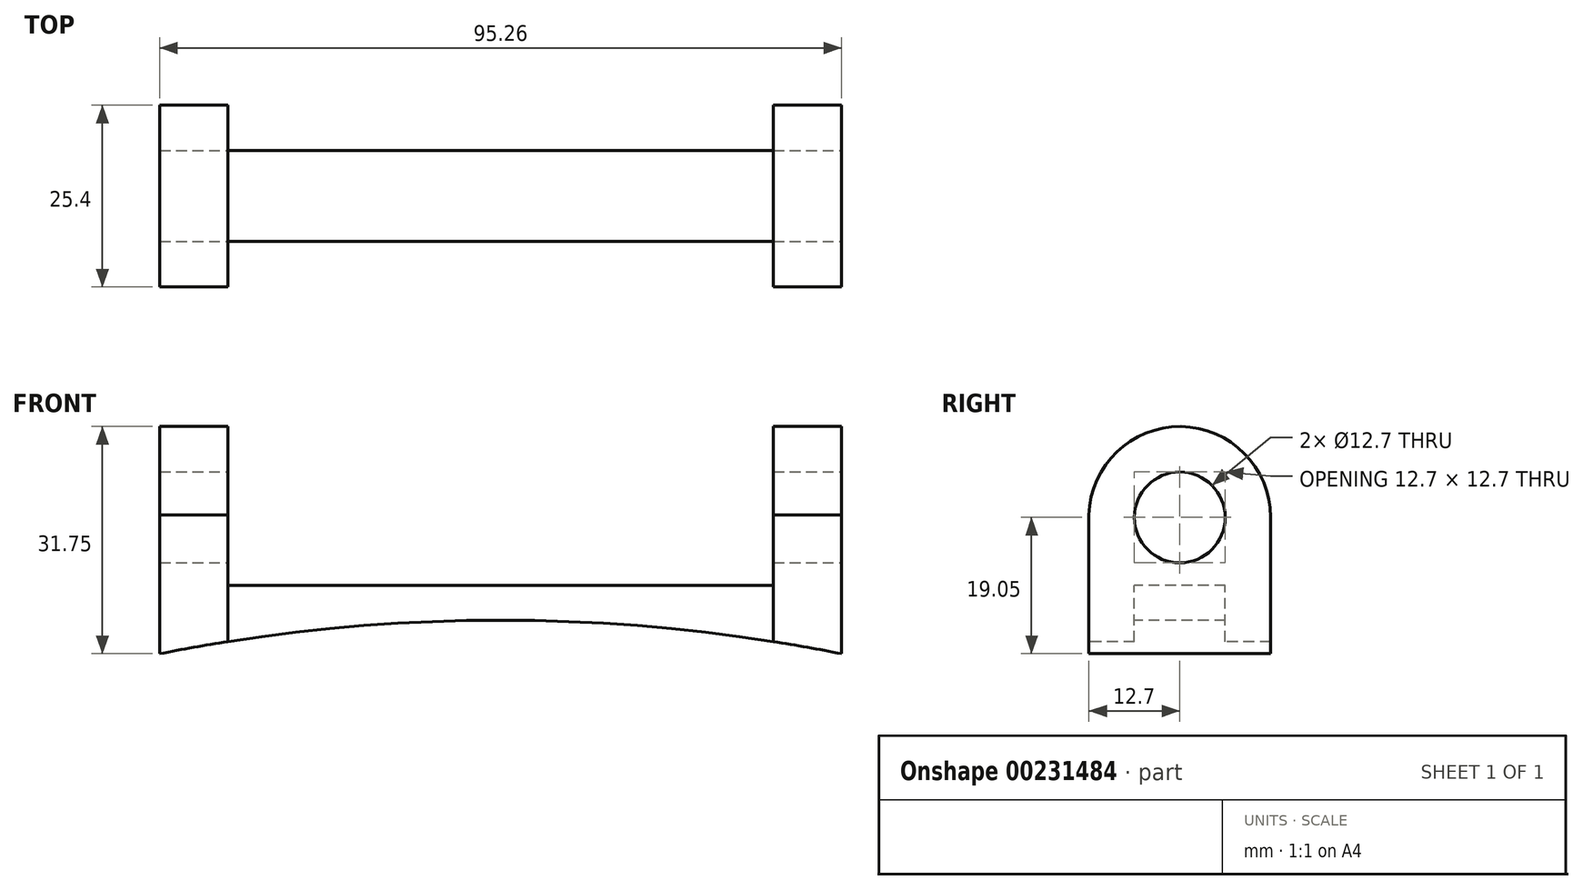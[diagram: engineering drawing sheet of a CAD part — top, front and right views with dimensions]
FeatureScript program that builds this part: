
annotation { "Feature Type Name" : "Feature", "Feature Type Description" : "" }
export const myFeature = defineFeature(function(context is Context, id is Id, definition is map)
    precondition{}
    {
        {
            var Q0;
            Q0=qCreatedBy(makeId("Front.planeOp"),FACE);
            var sketch = newSketch(context, id + "F0", { "sketchPlane" : qUnion([Q0])});
            skLineSegment(sketch, "E0", {"start": v(0, 0) * mm, "end": v(47.63, 0) * mm});
            skLineSegment(sketch, "E1", {"start": v(47.63, 0) * mm, "end": v(47.63, 31.75) * mm});
            skLineSegment(sketch, "E2", {"start": v(47.63, 31.75) * mm, "end": v(-47.62, 31.75) * mm});
            skLineSegment(sketch, "E3", {"start": v(-47.63, 31.75) * mm, "end": v(-47.63, 0) * mm});
            skLineSegment(sketch, "E4", {"start": v(-47.63, 0) * mm, "end": v(0, 0) * mm});
            skSolve(sketch);
        }
        {
            var Q0;
            Q0 = qSketchRegion(id + "F0", true);
            extrude(context, id + "F1", {"entities" : qUnion([Q0]), "depth" : 25.4 * mm});
        }
        {
            var Q0;
            Q0=makeQuery(id+"F1.opExtrude","CAP_FACE",FACE,{"disambiguationData":[OSD([sQuery(id+"F0.wireOp",EDGE,"E0"),sQuery(id+"F0.wireOp",EDGE,"E1"),sQuery(id+"F0.wireOp",EDGE,"E2"),sQuery(id+"F0.wireOp",EDGE,"E3"),sQuery(id+"F0.wireOp",EDGE,"E4")])],"isStart":false});
            var sketch = newSketch(context, id + "F2", { "sketchPlane" : qUnion([Q0])});
            skLineSegment(sketch, "E5.bottom", {"start": v(-38.1, 31.75) * mm, "end": v(38.1, 31.75) * mm});
            skLineSegment(sketch, "E5.top", {"start": v(-38.1, 9.52) * mm, "end": v(38.1, 9.52) * mm});
            skLineSegment(sketch, "E5.left", {"start": v(-38.1, 31.75) * mm, "end": v(-38.1, 9.52) * mm});
            skLineSegment(sketch, "E5.right", {"start": v(38.1, 31.75) * mm, "end": v(38.1, 9.52) * mm});
            skSolve(sketch);
        }
        {
            var Q0;
            Q0 = qSketchRegion(id + "F2", true);
            extrude(context, id + "F3", {"entities" : qUnion([Q0]), "operationType" : NewBodyOperationType.REMOVE, "oppositeDirection" : true, "depth" : 25.4 * mm});
        }
        {
            var Q0;
            Q0=makeQuery(id+"F3.boolean.opBoolean","COPY",FACE,{"derivedFrom":makeQuery(id+"F3.opExtrude","SWEPT_FACE",FACE,{"disambiguationData":[OSD([sQuery(id+"F2.wireOp",EDGE,"E5.top")])]})});
            var sketch = newSketch(context, id + "F4", { "sketchPlane" : qUnion([Q0])});
            skLineSegment(sketch, "E6.bottom", {"start": v(-38.1, 0) * mm, "end": v(38.1, 0) * mm});
            skLineSegment(sketch, "E6.top", {"start": v(-38.1, -6.35) * mm, "end": v(38.1, -6.35) * mm});
            skLineSegment(sketch, "E6.left", {"start": v(-38.1, 0) * mm, "end": v(-38.1, -6.35) * mm});
            skLineSegment(sketch, "E6.right", {"start": v(38.1, 0) * mm, "end": v(38.1, -6.35) * mm});
            skLineSegment(sketch, "E7.bottom", {"start": v(-38.1, -25.4) * mm, "end": v(38.1, -25.4) * mm});
            skLineSegment(sketch, "E7.top", {"start": v(-38.1, -19.05) * mm, "end": v(38.1, -19.05) * mm});
            skLineSegment(sketch, "E7.left", {"start": v(-38.1, -25.4) * mm, "end": v(-38.1, -19.05) * mm});
            skLineSegment(sketch, "E7.right", {"start": v(38.1, -25.4) * mm, "end": v(38.1, -19.05) * mm});
            skSolve(sketch);
        }
        {
            var Q0;
            Q0=makeQuery(id+"F1.opExtrude","CAP_FACE",FACE,{"disambiguationData":[OSD([sQuery(id+"F0.wireOp",EDGE,"E0"),sQuery(id+"F0.wireOp",EDGE,"E1"),sQuery(id+"F0.wireOp",EDGE,"E2"),sQuery(id+"F0.wireOp",EDGE,"E3"),sQuery(id+"F0.wireOp",EDGE,"E4")])],"isStart":false});
            var sketch = newSketch(context, id + "F5", { "sketchPlane" : qUnion([Q0])});
            skArc(sketch, "E8", {"start": v(47.63, 0) * mm, "mid": v(0, 4.68) * mm, "end": v(-47.62, 0) * mm});
            skLineSegment(sketch, "E9", {"start": v(-47.63, 0) * mm, "end": v(47.63, 0) * mm});
            skSolve(sketch);
        }
        {
            var Q0;
            Q0 = qSketchRegion(id + "F5", true);
            extrude(context, id + "F6", {"entities" : qUnion([Q0]), "operationType" : NewBodyOperationType.REMOVE, "oppositeDirection" : true, "depth" : 25.4 * mm});
        }
        {
            var Q0;
            Q0 = qSketchRegion(id + "F4", true);
            extrude(context, id + "F7", {"entities" : qUnion([Q0]), "operationType" : NewBodyOperationType.REMOVE, "oppositeDirection" : true, "depth" : 25.4 * mm});
        }
        {
            var Q0;
            Q0=makeQuery(id+"F1.opExtrude","SWEPT_FACE",FACE,{"disambiguationData":[OSD([sQuery(id+"F0.wireOp",EDGE,"E1")])]});
            var sketch = newSketch(context, id + "F8", { "sketchPlane" : qUnion([Q0])});
            skArc(sketch, "E10", {"start": v(0, 19.1) * mm, "mid": v(-12.9, 31.75) * mm, "end": v(-25.4, 18.7) * mm});
            skCircle(sketch, "E11", {"center": v(-12.7, 19.05) * mm, "radius": 6.35 * mm});
            skLineSegment(sketch, "E12", {"start": v(-25.4, 18.7) * mm, "end": v(-25.4, 31.75) * mm});
            skLineSegment(sketch, "E13", {"start": v(-25.4, 31.75) * mm, "end": v(0, 31.75) * mm});
            skLineSegment(sketch, "E14", {"start": v(0, 31.75) * mm, "end": v(0, 19.1) * mm});
            skSolve(sketch);
        }
        {
            var Q0;
            Q0 = qSketchRegion(id + "F8", true);
            extrude(context, id + "F9", {"entities" : qUnion([Q0]), "operationType" : NewBodyOperationType.REMOVE, "oppositeDirection" : true, "depth" : 95.25 * mm});
        }
    });
